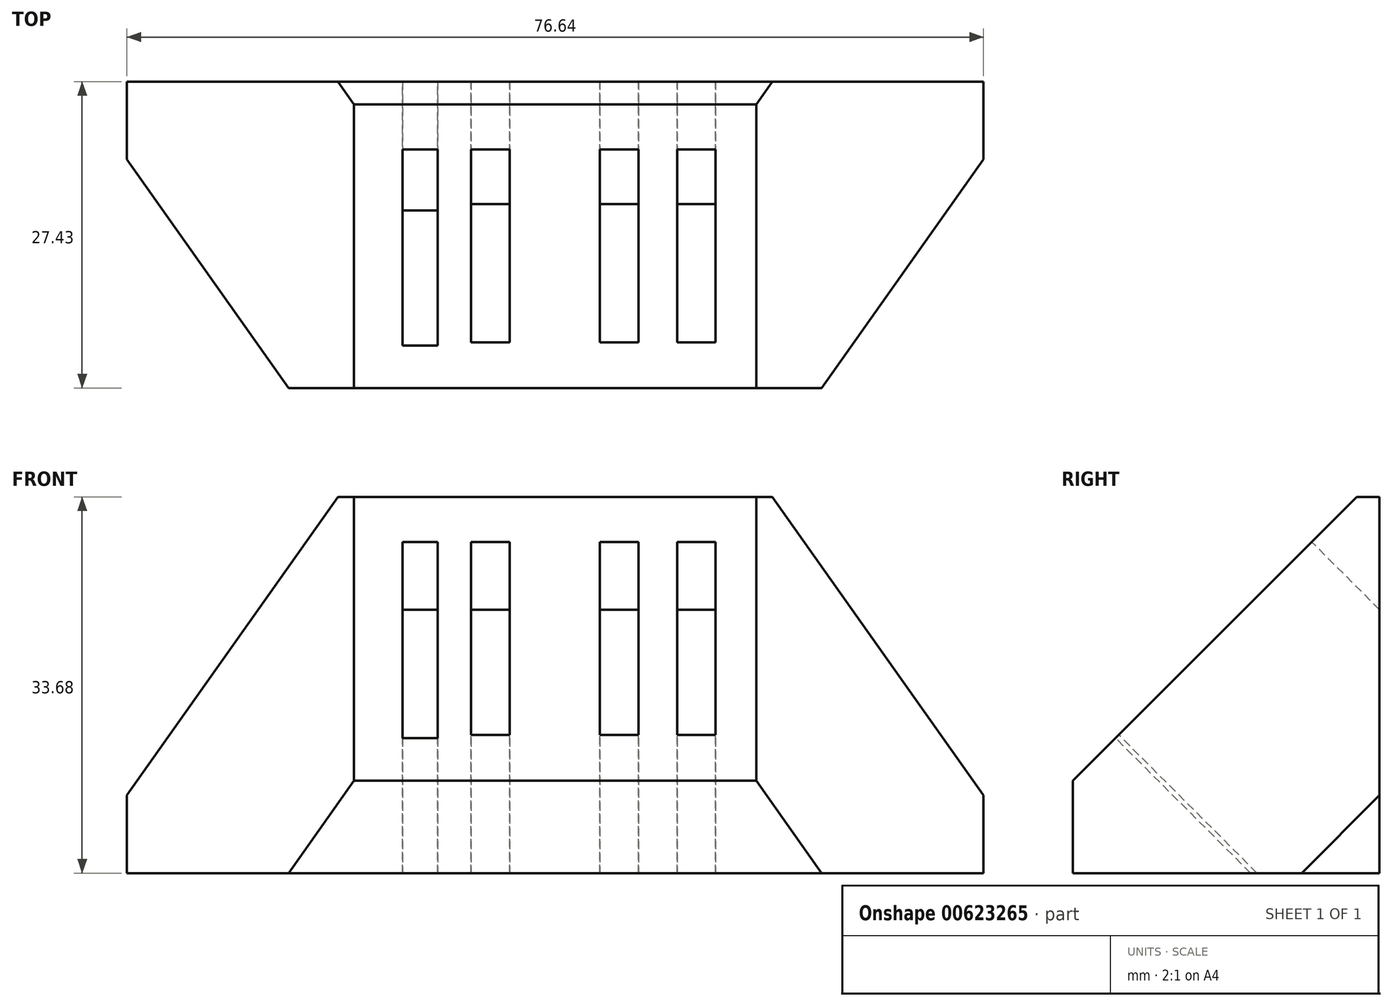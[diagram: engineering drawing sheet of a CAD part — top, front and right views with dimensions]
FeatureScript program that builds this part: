
annotation { "Feature Type Name" : "Feature", "Feature Type Description" : "" }
export const myFeature = defineFeature(function(context is Context, id is Id, definition is map)
    precondition{}
    {
        {
            var Q0;
            Q0=qCreatedBy(makeId("Front.planeOp"),FACE);
            var sketch = newSketch(context, id + "F0", { "sketchPlane" : qUnion([Q0])});
            skLineSegment(sketch, "E0.bottom", {"start": v(38.32, -16.84) * mm, "end": v(-38.32, -16.84) * mm});
            skLineSegment(sketch, "E0.top", {"start": v(38.32, 16.84) * mm, "end": v(-38.32, 16.84) * mm});
            skLineSegment(sketch, "E0.left", {"start": v(38.32, -16.84) * mm, "end": v(38.32, 16.84) * mm});
            skLineSegment(sketch, "E0.right", {"start": v(-38.32, -16.84) * mm, "end": v(-38.32, 16.84) * mm});
            skPoint(sketch, "E0.middle", {"position": v(0, 0) * mm});
            skSolve(sketch);
        }
        {
            var Q0;
            Q0=makeQuery(id+"F0.imprint","IMPRINT",FACE,{"disambiguationData":[TD([[makeQuery(id+"F0.imprint","IMPRINT",EDGE,{"derivedFrom":sQuery(id+"F0.wireOp",EDGE,"E0.bottom")}),-1.0]])]});
            extrude(context, id + "F1", {"entities" : qUnion([Q0]), "depth" : 27.43 * mm, "offsetDistance" : 25.4 * mm});
        }
        {
            var Q0;
            Q0=makeQuery(id+"F1.opExtrude","CAP_EDGE",EDGE,{"disambiguationData":[OSD([sQuery(id+"F0.wireOp",EDGE,"E0.top")])],"isStart":false});
            chamfer(context, id + "F2", {"entities" : qUnion([Q0]), "width" : 25.4 * mm, "tangentPropagation" : true});
        }
        {
            var Q0;
            Q0=makeQuery(id+"F2.opChamfer","BLEND_EDGE",EDGE,{"blendedFrom":[makeQuery(id+"F1.opExtrude","CAP_EDGE",EDGE,{"disambiguationData":[OSD([sQuery(id+"F0.wireOp",EDGE,"E0.top")])],"isStart":false}),makeQuery(id+"F1.opExtrude","SWEPT_FACE",FACE,{"disambiguationData":[OSD([sQuery(id+"F0.wireOp",EDGE,"E0.right")])]})],"blendedInto":[makeQuery(id+"F1.opExtrude","SWEPT_FACE",FACE,{"disambiguationData":[OSD([sQuery(id+"F0.wireOp",EDGE,"E0.right")])]})]});
            var Q1;
            Q1=makeQuery(id+"F2.opChamfer","BLEND_EDGE",EDGE,{"blendedFrom":[makeQuery(id+"F1.opExtrude","CAP_EDGE",EDGE,{"disambiguationData":[OSD([sQuery(id+"F0.wireOp",EDGE,"E0.top")])],"isStart":false}),makeQuery(id+"F1.opExtrude","SWEPT_FACE",FACE,{"disambiguationData":[OSD([sQuery(id+"F0.wireOp",EDGE,"E0.left")])]})],"blendedInto":[makeQuery(id+"F1.opExtrude","SWEPT_FACE",FACE,{"disambiguationData":[OSD([sQuery(id+"F0.wireOp",EDGE,"E0.left")])]})]});
            chamfer(context, id + "F3", {"entities" : qUnion([Q0, Q1]), "width" : 20.32 * mm, "tangentPropagation" : true});
        }
        {
            var Q0;
            Q0=makeQuery(id+"F2.opChamfer","BLEND_FACE",FACE,{"disambiguationData":[OSD([sQuery(id+"F0.wireOp",EDGE,"E0.top")])]});
            var sketch = newSketch(context, id + "F4", { "sketchPlane" : qUnion([Q0])});
            skLineSegment(sketch, "E1.bottom", {"start": v(-13.67, 4.77) * mm, "end": v(-10.5, 4.77) * mm});
            skLineSegment(sketch, "E1.top", {"start": v(-13.67, -20.06) * mm, "end": v(-10.5, -20.06) * mm});
            skLineSegment(sketch, "E1.left", {"start": v(-13.67, 4.77) * mm, "end": v(-13.67, -20.06) * mm});
            skLineSegment(sketch, "E1.right", {"start": v(-10.5, 4.77) * mm, "end": v(-10.5, -20.06) * mm});
            skSolve(sketch);
        }
        {
            var Q0;
            Q0 = qSketchRegion(id + "F4", true);
            extrude(context, id + "F5", {"entities" : qUnion([Q0]), "operationType" : NewBodyOperationType.REMOVE, "oppositeDirection" : true, "depth" : 25.4 * mm, "offsetDistance" : 25.4 * mm});
        }
        {
            var Q0;
            Q0=makeQuery(id+"F2.opChamfer","BLEND_FACE",FACE,{"disambiguationData":[OSD([sQuery(id+"F0.wireOp",EDGE,"E0.top")])]});
            var sketch = newSketch(context, id + "F6", { "sketchPlane" : qUnion([Q0])});
            skLineSegment(sketch, "E2.bottom", {"start": v(-7.52, 4.77) * mm, "end": v(-4.07, 4.77) * mm});
            skLineSegment(sketch, "E2.top", {"start": v(-7.52, -19.65) * mm, "end": v(-4.07, -19.65) * mm});
            skLineSegment(sketch, "E2.left", {"start": v(-7.52, 4.77) * mm, "end": v(-7.52, -19.65) * mm});
            skLineSegment(sketch, "E2.right", {"start": v(-4.07, 4.77) * mm, "end": v(-4.07, -19.65) * mm});
            skSolve(sketch);
        }
        {
            var Q0;
            Q0 = qSketchRegion(id + "F6", true);
            extrude(context, id + "F7", {"entities" : qUnion([Q0]), "operationType" : NewBodyOperationType.REMOVE, "oppositeDirection" : true, "depth" : 25.4 * mm, "offsetDistance" : 25.4 * mm});
        }
        {
            var Q0;
            Q0=makeQuery(id+"F2.opChamfer","BLEND_FACE",FACE,{"disambiguationData":[OSD([sQuery(id+"F0.wireOp",EDGE,"E0.top")])]});
            var sketch = newSketch(context, id + "F8", { "sketchPlane" : qUnion([Q0])});
            skLineSegment(sketch, "E3.bottom", {"start": v(14.35, 4.77) * mm, "end": v(10.9, 4.77) * mm});
            skLineSegment(sketch, "E3.top", {"start": v(14.35, -19.65) * mm, "end": v(10.9, -19.65) * mm});
            skLineSegment(sketch, "E3.left", {"start": v(14.35, 4.77) * mm, "end": v(14.35, -19.65) * mm});
            skLineSegment(sketch, "E3.right", {"start": v(10.9, 4.77) * mm, "end": v(10.9, -19.65) * mm});
            skSolve(sketch);
        }
        {
            var Q0;
            Q0 = qSketchRegion(id + "F8", true);
            extrude(context, id + "F9", {"entities" : qUnion([Q0]), "operationType" : NewBodyOperationType.REMOVE, "oppositeDirection" : true, "depth" : 25.4 * mm, "offsetDistance" : 25.4 * mm});
        }
        {
            var Q0;
            Q0=makeQuery(id+"F2.opChamfer","BLEND_FACE",FACE,{"disambiguationData":[OSD([sQuery(id+"F0.wireOp",EDGE,"E0.top")])]});
            var sketch = newSketch(context, id + "F10", { "sketchPlane" : qUnion([Q0])});
            skLineSegment(sketch, "E4.bottom", {"start": v(7.44, 4.77) * mm, "end": v(4, 4.77) * mm});
            skLineSegment(sketch, "E4.top", {"start": v(7.44, -19.65) * mm, "end": v(4, -19.65) * mm});
            skLineSegment(sketch, "E4.left", {"start": v(7.44, 4.77) * mm, "end": v(7.44, -19.65) * mm});
            skLineSegment(sketch, "E4.right", {"start": v(4, 4.77) * mm, "end": v(4, -19.65) * mm});
            skSolve(sketch);
        }
        {
            var Q0;
            Q0 = qSketchRegion(id + "F10", true);
            extrude(context, id + "F11", {"entities" : qUnion([Q0]), "operationType" : NewBodyOperationType.REMOVE, "oppositeDirection" : true, "depth" : 25.4 * mm, "offsetDistance" : 25.4 * mm});
        }
    });
